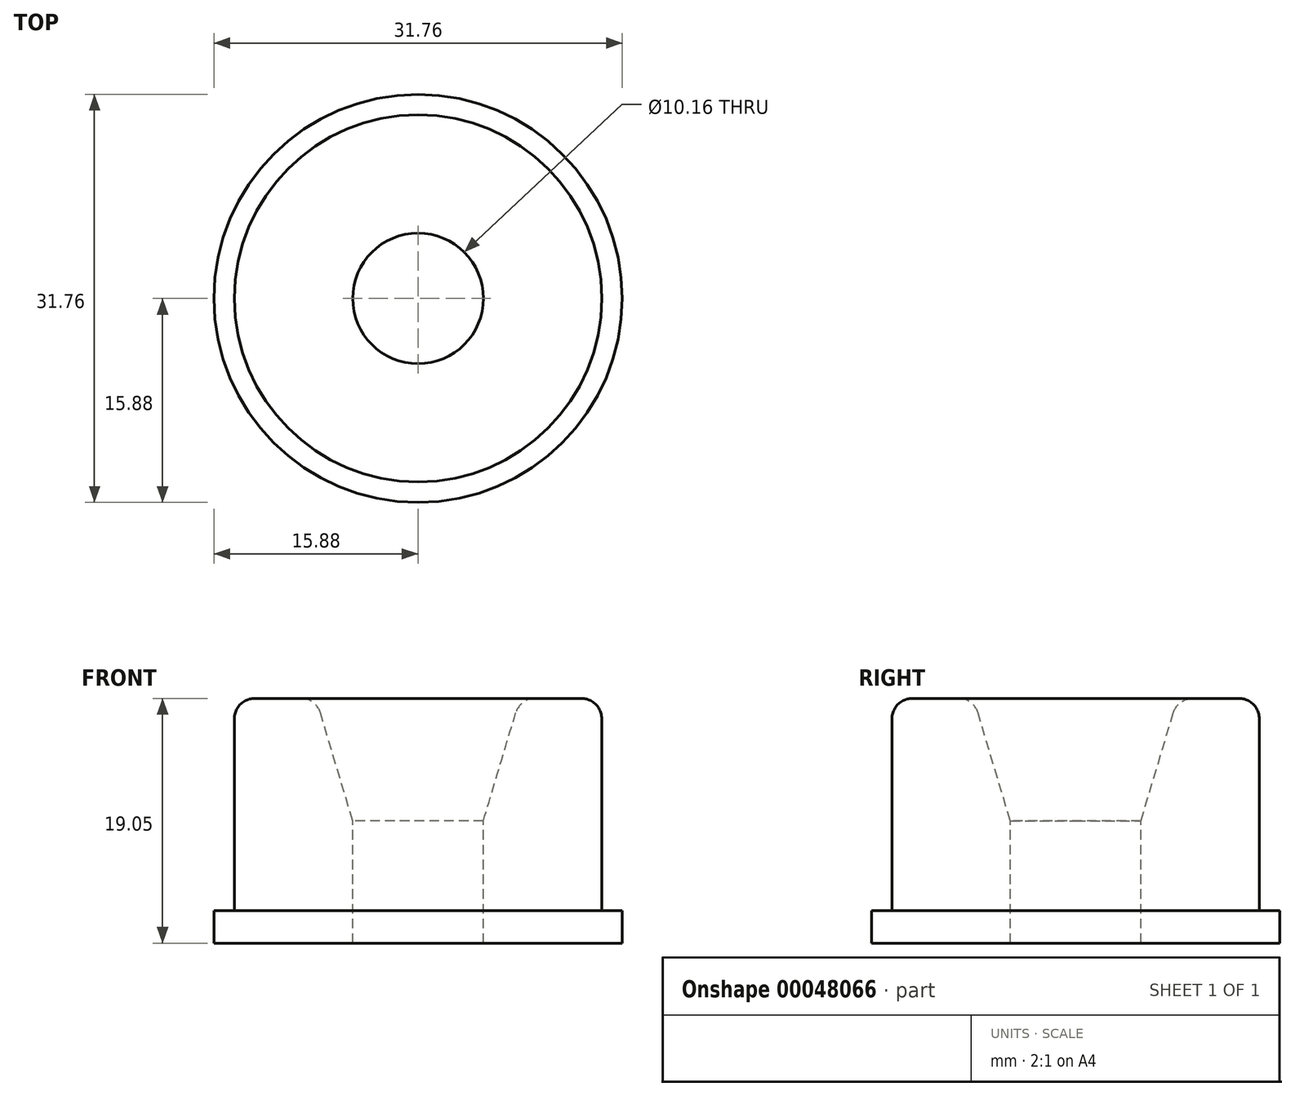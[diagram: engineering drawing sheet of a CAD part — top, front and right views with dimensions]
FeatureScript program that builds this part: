
annotation { "Feature Type Name" : "Feature", "Feature Type Description" : "" }
export const myFeature = defineFeature(function(context is Context, id is Id, definition is map)
    precondition{}
    {
        {
            var Q0;
            Q0=qCreatedBy(makeId("Top.planeOp"),FACE);
            var sketch = newSketch(context, id + "F0", { "sketchPlane" : qUnion([Q0])});
            skCircle(sketch, "E0", {"center": v(0, 0) * mm, "radius": 14.29 * mm});
            skSolve(sketch);
        }
        {
            var Q0;
            Q0 = qSketchRegion(id + "F0", true);
            extrude(context, id + "F1", {"entities" : qUnion([Q0]), "depth" : 19.05 * mm});
        }
        {
            var Q0;
            Q0=makeQuery(id+"F1.opExtrude","CAP_FACE",FACE,{"disambiguationData":[OSD([sQuery(id+"F0.wireOp",EDGE,"E0")])],"isStart":true});
            var sketch = newSketch(context, id + "F2", { "sketchPlane" : qUnion([Q0])});
            skCircle(sketch, "E1", {"center": v(0, 0) * mm, "radius": 15.88 * mm});
            skSolve(sketch);
        }
        {
            var Q0;
            Q0 = qSketchRegion(id + "F2", true);
            extrude(context, id + "F3", {"entities" : qUnion([Q0]), "operationType" : NewBodyOperationType.ADD, "oppositeDirection" : true, "depth" : 2.54 * mm});
        }
        {
            var Q0;
            Q0=qCreatedBy(makeId("Front.planeOp"),FACE);
            var sketch = newSketch(context, id + "F4", { "sketchPlane" : qUnion([Q0])});
            skLineSegment(sketch, "E2", {"start": v(0, 0) * mm, "end": v(0, 19.05) * mm});
            skLineSegment(sketch, "E3", {"start": v(7.94, 19.05) * mm, "end": v(5.08, 9.53) * mm});
            skLineSegment(sketch, "E4", {"start": v(5.08, 9.53) * mm, "end": v(5.08, 0) * mm});
            skLineSegment(sketch, "E5", {"start": v(5.08, 0) * mm, "end": v(0, 0) * mm});
            skLineSegment(sketch, "E6.0", {"start": v(0, 19.05) * mm, "end": v(7.94, 19.05) * mm});
            skPoint(sketch, "E7.orphan", {"position": v(14.29, 19.05) * mm});
            skPoint(sketch, "E8.orphan", {"position": v(-14.29, 19.05) * mm});
            skSolve(sketch);
        }
        {
            var Q0;
            Q0 = qSketchRegion(id + "F4", true);
            var Q1;
            Q1=sQuery(id+"F4.wireOp",EDGE,"E2");
            revolve(context, id + "F5", {"operationType" : NewBodyOperationType.REMOVE, "entities" : qUnion([Q0]), "axis" : qUnion([Q1]), "revolveType" : RevolveType.FULL, "oppositeDirection" : true});
        }
        {
            var Q0;
            Q0=makeQuery(id+"F1.opExtrude","CAP_FACE",FACE,{"disambiguationData":[OSD([sQuery(id+"F0.wireOp",EDGE,"E0")])],"isStart":false});
            var Q1;
            Q1=makeQuery(id+"F5.boolean.opBoolean","COPY",EDGE,{"derivedFrom":makeQuery(id+"F5.opRevolve","SWEPT_EDGE",EDGE,{"disambiguationData":[OSD([sQuery(id+"F4.wireOp",EDGE,"E4"),sQuery(id+"F4.wireOp",EDGE,"E5")])]})});
            fillet(context, id + "F6", {"entities" : qUnion([Q0, Q1]), "radius" : 1.59 * mm, "tangentPropagation" : true, "allowEdgeOverflow" : false});
        }
    });
